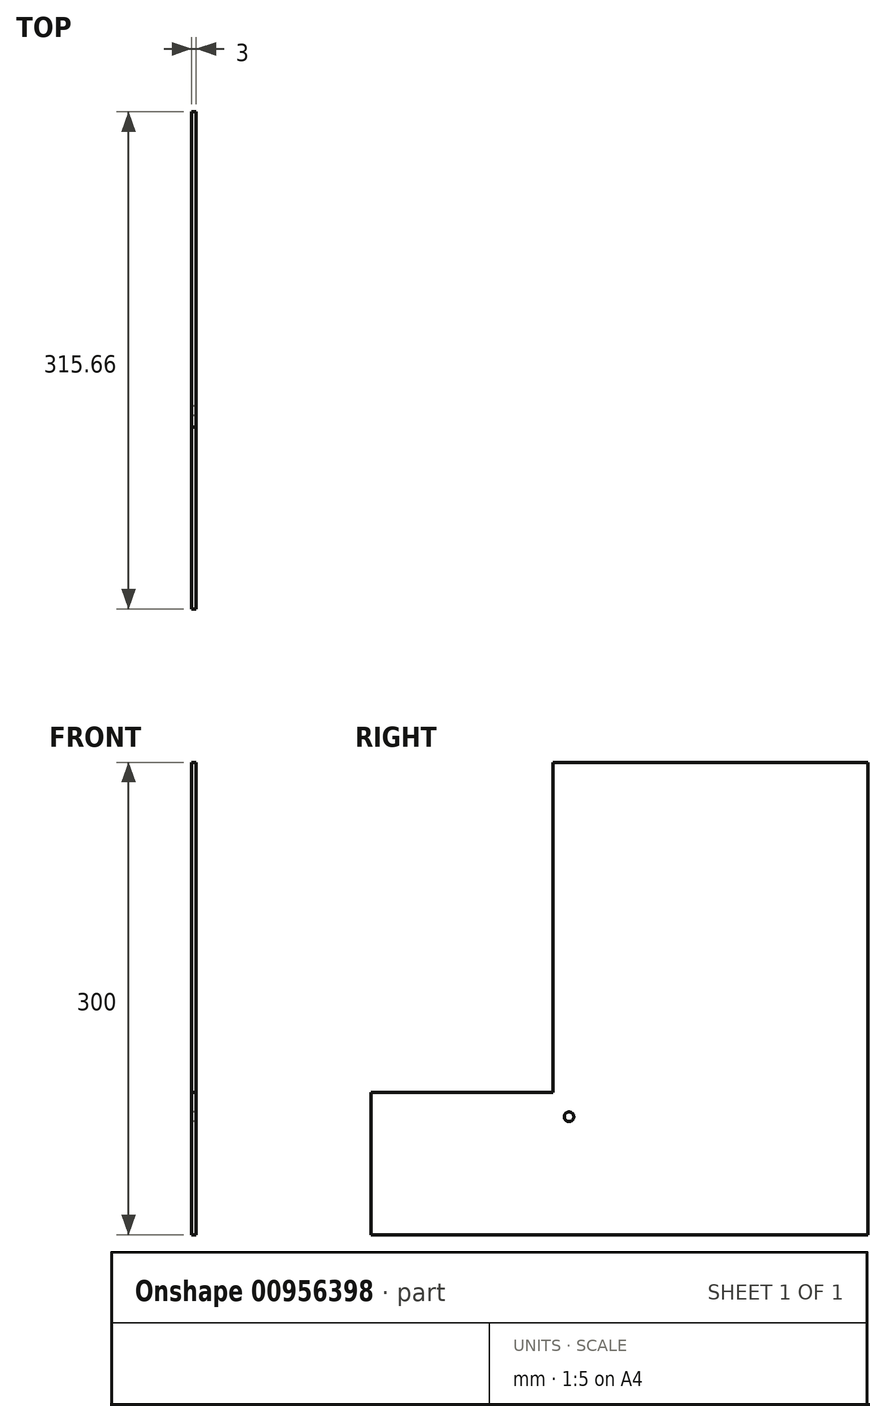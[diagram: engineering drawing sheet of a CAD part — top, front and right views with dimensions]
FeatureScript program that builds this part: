
annotation { "Feature Type Name" : "Feature", "Feature Type Description" : "" }
export const myFeature = defineFeature(function(context is Context, id is Id, definition is map)
    precondition{}
    {
        {
            var Q0;
            Q0=qCreatedBy(makeId("Right.planeOp"),FACE);
            var sketch = newSketch(context, id + "F0", { "sketchPlane" : qUnion([Q0])});
            skLineSegment(sketch, "E0", {"start": v(0, 0) * mm, "end": v(0, 300) * mm});
            skLineSegment(sketch, "E1", {"start": v(0, 0) * mm, "end": v(200.05, 0) * mm});
            skLineSegment(sketch, "E2", {"start": v(200.05, 0) * mm, "end": v(200.05, 300) * mm});
            skLineSegment(sketch, "E3", {"start": v(200.05, 300) * mm, "end": v(0, 300) * mm});
            skLineSegment(sketch, "E4", {"start": v(0, 0) * mm, "end": v(-115.6, 0) * mm});
            skLineSegment(sketch, "E5", {"start": v(-115.6, 0) * mm, "end": v(-115.6, 90.5) * mm});
            skLineSegment(sketch, "E6", {"start": v(-115.6, 90.5) * mm, "end": v(0, 90.5) * mm});
            skLineSegment(sketch, "E7.left", {"start": v(0, 90.5) * mm, "end": v(0, 74.86) * mm});
            skCircle(sketch, "E8", {"center": v(10.26, 74.86) * mm, "radius": 3.02 * mm});
            skSolve(sketch);
        }
        {
            var Q0;
            {var subQ0=sQuery(id+"F0.wireOp",EDGE,"E1");Q0=makeQuery(id+"F0.imprint","IMPRINT",FACE,{"disambiguationData":[TD([[makeQuery(id+"F0.imprint","IMPRINT",EDGE,{"derivedFrom":subQ0}),1.0]])]});}
            var Q1;
            {var subQ0=sQuery(id+"F0.wireOp",EDGE,"E4");Q1=makeQuery(id+"F0.imprint","IMPRINT",FACE,{"disambiguationData":[TD([[makeQuery(id+"F0.imprint","IMPRINT",EDGE,{"derivedFrom":subQ0}),-1.0]])]});}
            extrude(context, id + "F1", {"entities" : qUnion([Q0, Q1]), "depth" : 3 * mm, "offsetDistance" : 25 * mm});
        }
    });
